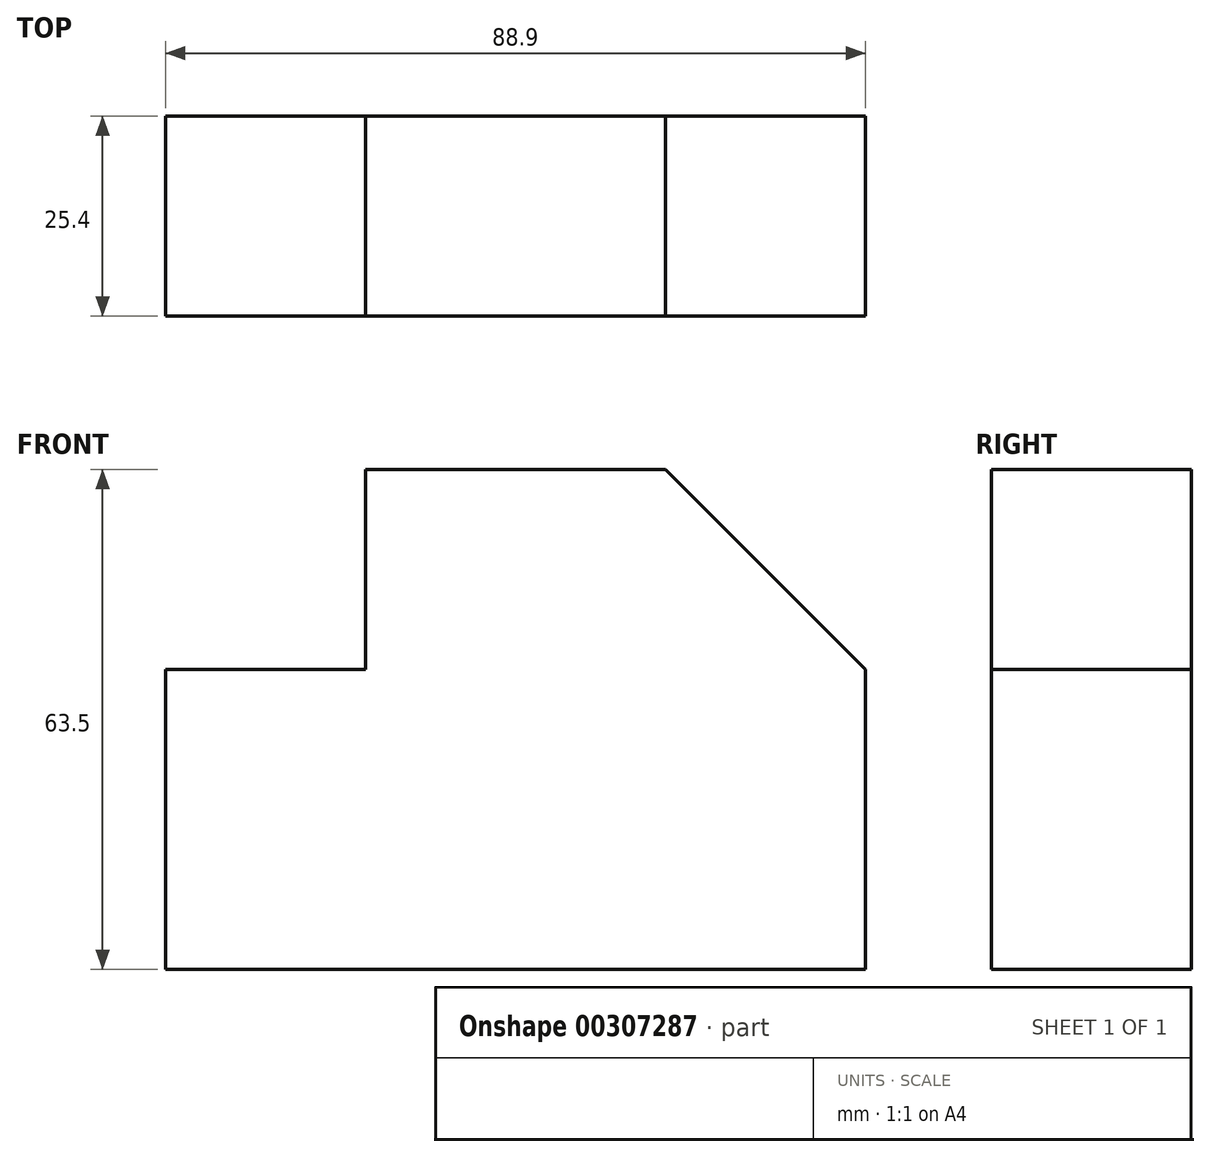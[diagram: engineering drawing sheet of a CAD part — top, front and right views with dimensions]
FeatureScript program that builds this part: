
annotation { "Feature Type Name" : "Feature", "Feature Type Description" : "" }
export const myFeature = defineFeature(function(context is Context, id is Id, definition is map)
    precondition{}
    {
        {
            var Q0;
            Q0=qCreatedBy(makeId("Front.planeOp"),FACE);
            var sketch = newSketch(context, id + "F0", { "sketchPlane" : qUnion([Q0])});
            skLineSegment(sketch, "E0", {"start": v(-40.65, -23.57) * mm, "end": v(48.25, -23.57) * mm});
            skLineSegment(sketch, "E1", {"start": v(48.25, -23.57) * mm, "end": v(48.25, 14.53) * mm});
            skLineSegment(sketch, "E2", {"start": v(48.25, 14.53) * mm, "end": v(22.85, 39.93) * mm});
            skLineSegment(sketch, "E3", {"start": v(22.85, 39.93) * mm, "end": v(-15.25, 39.93) * mm});
            skLineSegment(sketch, "E4", {"start": v(-15.25, 39.93) * mm, "end": v(-15.25, 14.53) * mm});
            skLineSegment(sketch, "E5", {"start": v(-15.25, 14.53) * mm, "end": v(-40.65, 14.53) * mm});
            skLineSegment(sketch, "E6", {"start": v(-40.65, 14.53) * mm, "end": v(-40.65, -23.57) * mm});
            skSolve(sketch);
        }
        {
            var Q0;
            Q0=makeQuery(id+"F0.imprint","IMPRINT",FACE,{"disambiguationData":[TD([[makeQuery(id+"F0.imprint","IMPRINT",EDGE,{"derivedFrom":sQuery(id+"F0.wireOp",EDGE,"E0")}),1.0]])]});
            extrude(context, id + "F1", {"entities" : qUnion([Q0]), "depth" : 25.4 * mm});
        }
    });
